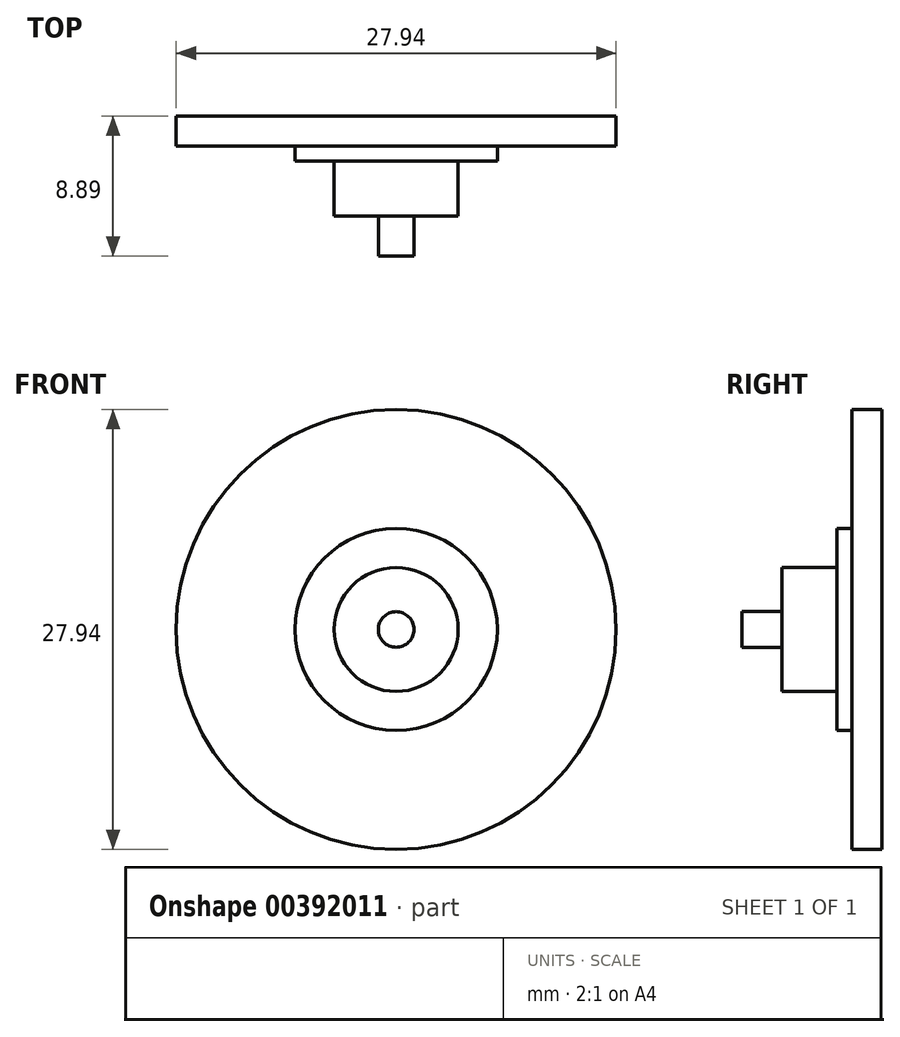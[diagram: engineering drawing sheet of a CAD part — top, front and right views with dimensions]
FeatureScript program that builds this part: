
annotation { "Feature Type Name" : "Feature", "Feature Type Description" : "" }
export const myFeature = defineFeature(function(context is Context, id is Id, definition is map)
    precondition{}
    {
        {
            var Q0;
            Q0=qCreatedBy(makeId("Right.planeOp"),FACE);
            var sketch = newSketch(context, id + "F0", { "sketchPlane" : qUnion([Q0])});
            skLineSegment(sketch, "E0", {"start": v(0, 0) * mm, "end": v(34.7, 0) * mm, "construction": true});
            skLineSegment(sketch, "E1", {"start": v(-2.54, 1.13) * mm, "end": v(0, 1.13) * mm});
            skLineSegment(sketch, "E2", {"start": v(-2.54, 1.13) * mm, "end": v(-2.54, 0) * mm});
            skLineSegment(sketch, "E3", {"start": v(-2.54, 0) * mm, "end": v(6.35, 0) * mm});
            skLineSegment(sketch, "E4", {"start": v(6.35, 0) * mm, "end": v(6.35, 13.97) * mm});
            skLineSegment(sketch, "E5", {"start": v(6.35, 13.97) * mm, "end": v(4.45, 13.97) * mm});
            skLineSegment(sketch, "E6", {"start": v(4.45, 13.97) * mm, "end": v(4.45, 6.42) * mm});
            skLineSegment(sketch, "E7", {"start": v(3.5, 3.94) * mm, "end": v(0, 3.94) * mm});
            skLineSegment(sketch, "E8", {"start": v(0, 3.94) * mm, "end": v(0, 1.13) * mm});
            skPoint(sketch, "E9.orphan", {"position": v(2.54, 1.13) * mm});
            skLineSegment(sketch, "E10", {"start": v(3.5, 3.94) * mm, "end": v(3.5, 6.42) * mm});
            skLineSegment(sketch, "E11", {"start": v(3.5, 6.42) * mm, "end": v(4.45, 6.42) * mm});
            skSolve(sketch);
        }
        {
            var Q0;
            Q0=qSketchRegion(id+"F0",true);
            var Q1;
            Q1=sQuery(id+"F0.wireOp",EDGE,"E0");
            revolve(context, id + "F1", {"entities" : qUnion([Q0]), "axis" : qUnion([Q1]), "revolveType" : RevolveType.FULL});
        }
    });
